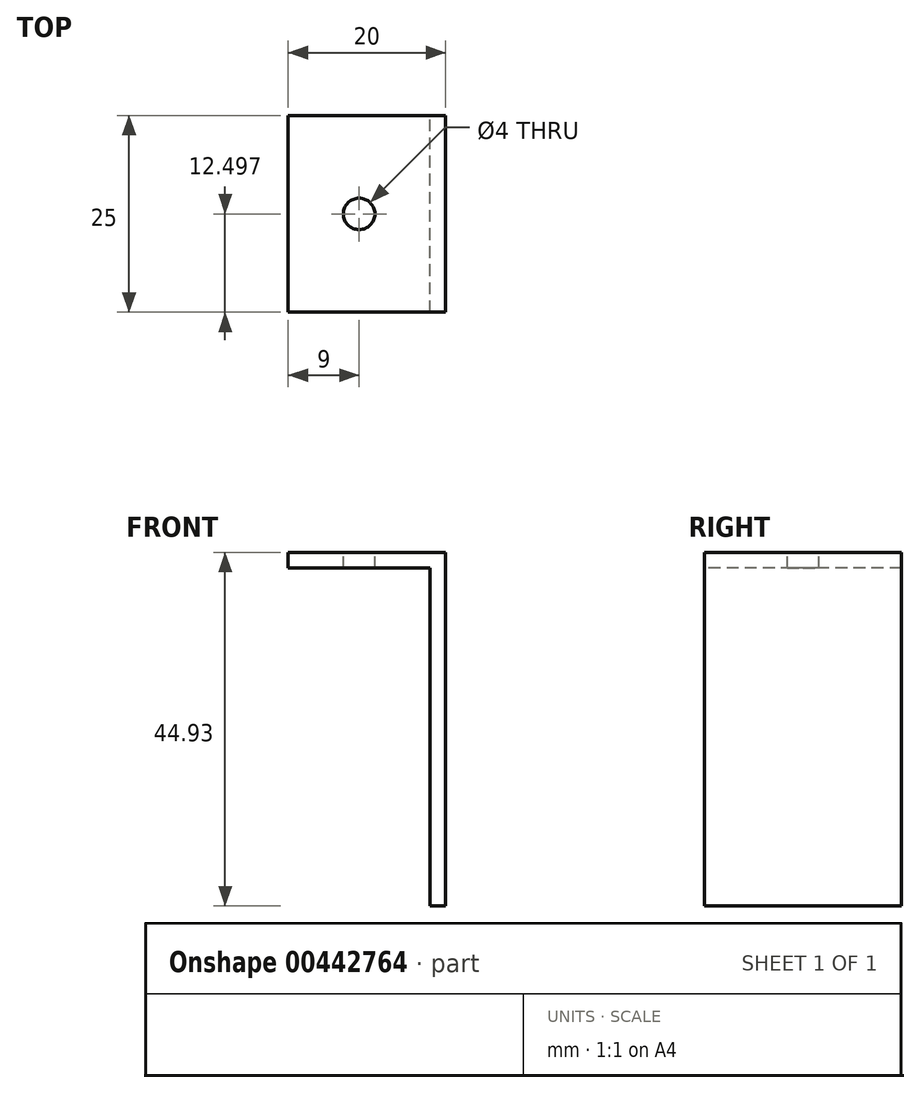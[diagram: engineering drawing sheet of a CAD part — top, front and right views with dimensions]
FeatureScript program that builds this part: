
annotation { "Feature Type Name" : "Feature", "Feature Type Description" : "" }
export const myFeature = defineFeature(function(context is Context, id is Id, definition is map)
    precondition{}
    {
        {
            var Q0;
            Q0=qCreatedBy(makeId("Top.planeOp"),FACE);
            var sketch = newSketch(context, id + "F0", { "sketchPlane" : qUnion([Q0])});
            skLineSegment(sketch, "E0", {"start": v(-18, 22.5) * mm, "end": v(0, 22.5) * mm});
            skLineSegment(sketch, "E1", {"start": v(-18, 22.5) * mm, "end": v(-18, -2.5) * mm});
            skLineSegment(sketch, "E2", {"start": v(-18, -2.5) * mm, "end": v(0, -2.5) * mm});
            skLineSegment(sketch, "E3", {"start": v(0, -2.5) * mm, "end": v(0, 22.5) * mm});
            skCircle(sketch, "E4", {"center": v(-9, 10) * mm, "radius": 2 * mm});
            skPoint(sketch, "E4.centerSnap0", {"position": v(-9, -2.5) * mm});
            skPoint(sketch, "E4.centerSnap1", {"position": v(-18, 10) * mm});
            skSolve(sketch);
        }
        {
            var Q0;
            Q0 = qSketchRegion(id + "F0", true);
            extrude(context, id + "F1", {"entities" : qUnion([Q0]), "oppositeDirection" : true, "depth" : 2 * mm});
        }
        {
            var Q0;
            Q0=qCreatedBy(makeId("Right.planeOp"),FACE);
            var sketch = newSketch(context, id + "F2", { "sketchPlane" : qUnion([Q0])});
            skLineSegment(sketch, "E5.0", {"start": v(-2.5, 0) * mm, "end": v(22.5, 0) * mm});
            skLineSegment(sketch, "E6", {"start": v(-2.5, 0) * mm, "end": v(-2.5, -44.93) * mm});
            skLineSegment(sketch, "E7", {"start": v(-2.5, -44.93) * mm, "end": v(22.5, -44.93) * mm});
            skLineSegment(sketch, "E8", {"start": v(22.5, -44.93) * mm, "end": v(22.5, 0) * mm});
            skSolve(sketch);
        }
        {
            var Q0;
            Q0 = qSketchRegion(id + "F2", true);
            extrude(context, id + "F3", {"entities" : qUnion([Q0]), "operationType" : NewBodyOperationType.ADD, "depth" : 2 * mm});
        }
    });
